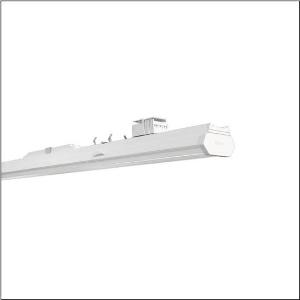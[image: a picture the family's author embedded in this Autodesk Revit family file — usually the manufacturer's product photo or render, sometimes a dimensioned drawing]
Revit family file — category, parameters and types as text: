
# Revit family: licross_r__11_protected_ho_51td12cn4exm_9b5e
name_source: partatom
category: Lighting Fixtures
units: mm (PartAtom-declared; Revit-internal decimal feet)

## family parameters
Cut with Voids When Loaded = No
Host = Face
Light Source = No
Part Type = Normal
Room Calculation Point = No
Round Connector Dimension = Use Diameter
Shared = No

## types (1)
- --- (1 x LED, 14240 lm, 77.6 W, 4000K)
    Apparent Load = 78 VA
    CIE Flux Codes = 70 91 97 98 100
    Color Rendering = 80
    Color Temperature = 4000K
    Default Elevation = 1800 mm
    Description = Licross® 11 Protected HO, luminaire insert, of sheet steel, galvanised, coil coated, white, length: 1.500mm, width: 90mm, height: 101mm, LED rated luminous flux: 14.240lm, light colour: 840, control gear: ON/OFF Multilumen, CLOi, with plug, 3-pole, with phase selection, mains connection: 220..240V, AC, 50/60Hz, start of lifetime: 78W, end of service life: 87W, halogen-free wiring, primary light control with lens, of plastic, primary optical cover: cover, of PMMA, light emission: direct distribution, primary light characteristic: symmetric, protection rating (complete): IP54, insulation class (complete): insulation class I (protective earthing), certification: CE, ENEC, VDE, UKCA, protection symbol: D if used in an environment with non-conductive dust loads with corresponding accessories, impact resistance: IK06, permissible ambient temperature for indoor applications: -35..+35°C, corresponds to IFS (International Featured Standards) requirements for safety and quality in the food industry, reducing of maximum allowable ambient temperature of 5°C with ceiling mounting, LABS conformity tested according to VDMA 24364:2018-05, packaging unit: 1 piece
    Height = 92 mm
    Lamp = 1 x LED
    Lamp Light Flux = 14240 lm
    Lamp Power = 77.6 W
    Lamp count = 1
    Length = 1500 mm
    Luminous efficacy = 184 lm/W
    Manufacturer = Siteco
    ModVariant = No
    Model = 51TD12CN4EXM
    Mounting Place = Ceiling
    Mounting Type = Pendant
    Number of Poles = 1
    OnlyDefault = Yes
    Power Factor = 1
    Product Name = Licross® 11 Protected HO
    Product group = luminaire insert
    ProductGroupID = 901
    Protection Class = Protection class I
    Protection Degree = IP 54
    RLX_Detail_Level = 1
    RLX_Emergency_Light_Flux = 0 lm
    RLX_Emergency_Type = 0
    RLX_Emergency_Type_DB = No
    RlxData = <blob elided: 22177 chars, md5=fe3e970a>
    Socket = socket
    Standby Power = 0 W
    System Light Flux = 14240 lm
    System Power = 78 W
    Type Comments = factory setting: luminous flux: 100 % | (A | C | E) | 181 mA
    Type Image = l_1256145.jpg
    URL = http://relux.com
    VarID = @adj_019479
    Voltage = 0 V
    Weight = 0.00 kg
    Width = 88 mm

## geometry (parser evidence)
native form markers: Blend x4, Sweep x11
no freeform markers — native parametric forms only
